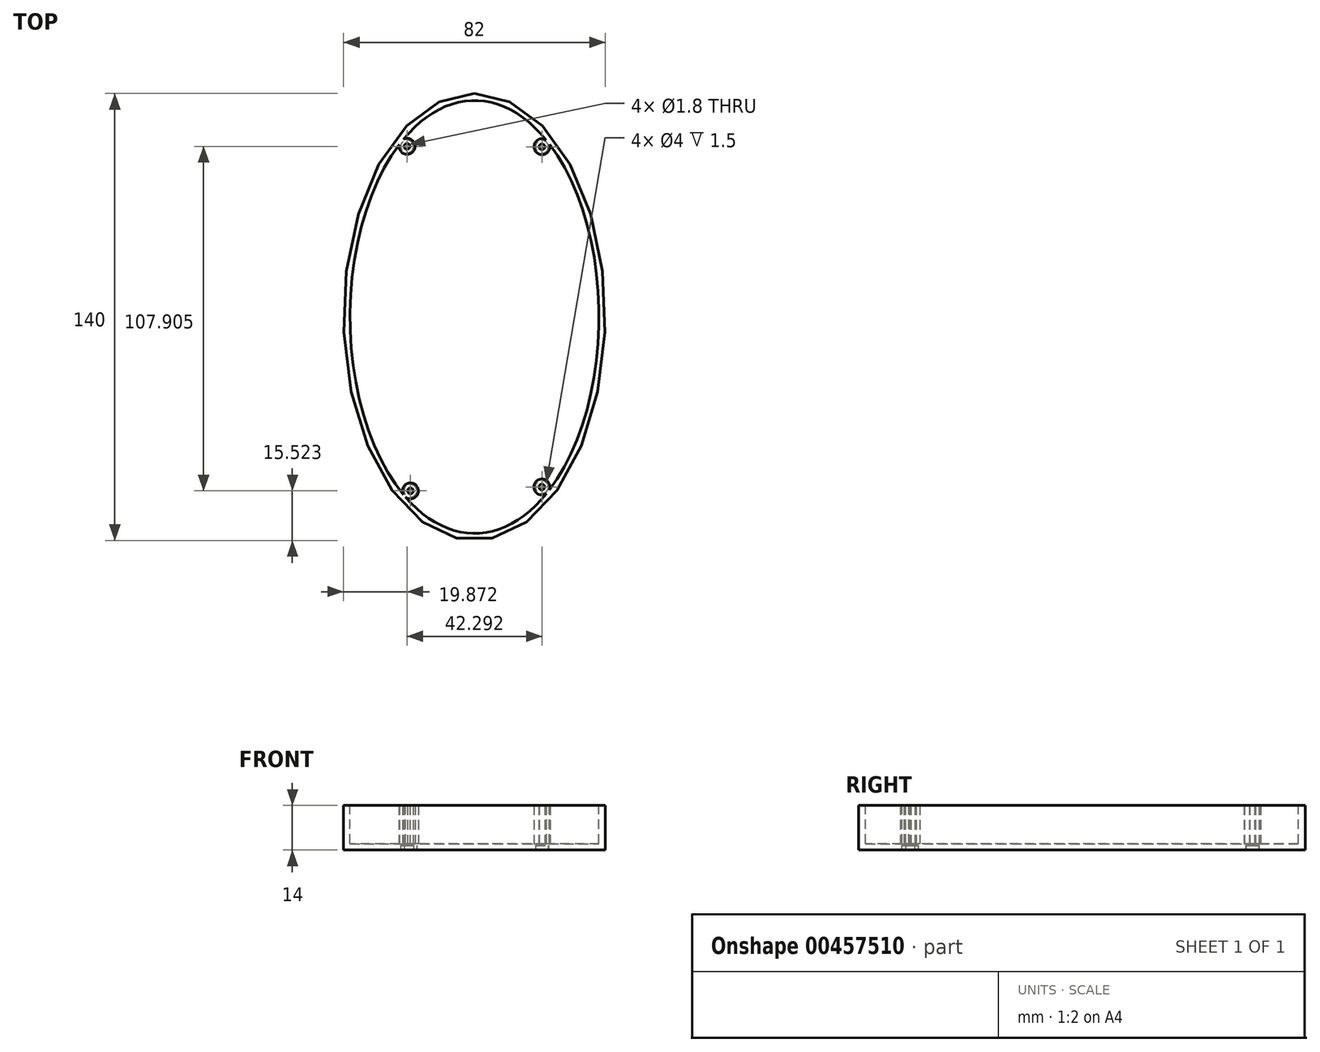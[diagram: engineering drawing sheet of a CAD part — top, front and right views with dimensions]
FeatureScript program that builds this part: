
annotation { "Feature Type Name" : "Feature", "Feature Type Description" : "" }
export const myFeature = defineFeature(function(context is Context, id is Id, definition is map)
    precondition{}
    {
        {
            var Q0;
            Q0=qCreatedBy(makeId("Top.planeOp"),FACE);
            var sketch = newSketch(context, id + "F0", { "sketchPlane" : qUnion([Q0])});
            skEllipse(sketch, "E0", {"center": v(-6.22, 3.26) * mm, "majorRadius": 70 * mm, "minorRadius": 41 * mm, "majorAxis": v(0, 1)});
            skSolve(sketch);
        }
        {
            var Q0;
            Q0 = qSketchRegion(id + "F2", true);
            var Q1;
            Q1 = qSketchRegion(id + "F0", true);
            extrude(context, id + "F1", {"entities" : qUnion([Q0, Q1]), "depth" : 17 * mm, "offsetDistance" : 25 * mm});
        }
        {
            var Q0;
            Q0=makeQuery(id+"F1.opExtrude","CAP_FACE",FACE,{"disambiguationData":[OSD([sQuery(id+"F0.wireOp",EDGE,"E0")])],"isStart":false});
            var sketch = newSketch(context, id + "F2", { "sketchPlane" : qUnion([Q0])});
            skEllipse(sketch, "E1", {"center": v(-6.22, 3.26) * mm, "majorRadius": 67.8 * mm, "minorRadius": 39 * mm, "majorAxis": v(0, 1)});
            skSolve(sketch);
        }
        {
            var Q0;
            Q0=makeQuery(id+"F2.imprint","IMPRINT",FACE,{"disambiguationData":[TD([[makeQuery(id+"F2.imprint","IMPRINT",EDGE,{"derivedFrom":sQuery(id+"F2.wireOp",EDGE,"E1")}),1.0]])]});
            extrude(context, id + "F3", {"entities" : qUnion([Q0]), "operationType" : NewBodyOperationType.REMOVE, "oppositeDirection" : true, "depth" : 15 * mm});
        }
        {
            var Q0;
            Q0=makeQuery(id+"F3.boolean.opBoolean","COPY",FACE,{"derivedFrom":makeQuery(id+"F3.opExtrude","CAP_FACE",FACE,{"disambiguationData":[OSD([sQuery(id+"F2.wireOp",EDGE,"E1")])],"isStart":false})});
            var sketch = newSketch(context, id + "F4", { "sketchPlane" : qUnion([Q0])});
            skCircle(sketch, "E2", {"center": v(-27.35, 56.69) * mm, "radius": 2.5 * mm});
            skPoint(sketch, "E2.first.point", {"position": v(-28.49, 58.91) * mm});
            skPoint(sketch, "E2.second.point", {"position": v(-26.1, 54.53) * mm});
            skPoint(sketch, "E2.third.point", {"position": v(-27.44, 54.19) * mm});
            skCircle(sketch, "E3", {"center": v(-27.35, 56.69) * mm, "radius": 0.9 * mm});
            skSolve(sketch);
        }
        {
            var Q0;
            {var subQ0=sQuery(id+"F4.wireOp",EDGE,"E2");var subQ1=makeQuery(id+"F3.boolean.opBoolean","COPY",EDGE,{"derivedFrom":makeQuery(id+"F3.opExtrude","CAP_EDGE",EDGE,{"disambiguationData":[OSD([sQuery(id+"F2.wireOp",EDGE,"E1")])],"isStart":false})});var subQ2=makeQuery(id+"F4.imprint","INTERSECT",VERTEX,{"disambiguationData":[OD(0.0)],"derivedFrom":[subQ1,subQ0]});Q0=makeQuery(id+"F4.imprint","IMPRINT",FACE,{"disambiguationData":[TD([[makeQuery(id+"F4.imprint","IMPRINT",EDGE,{"disambiguationData":[TD([[subQ2,-1.0]])],"derivedFrom":subQ0}),1.0]])]});}
            extrude(context, id + "F5", {"entities" : qUnion([Q0]), "operationType" : NewBodyOperationType.ADD, "depth" : 15 * mm});
        }
        {
            var Q0;
            Q0=makeQuery(id+"F3.boolean.opBoolean","COPY",FACE,{"derivedFrom":makeQuery(id+"F3.opExtrude","CAP_FACE",FACE,{"disambiguationData":[OSD([sQuery(id+"F2.wireOp",EDGE,"E1")])],"isStart":false})});
            var sketch = newSketch(context, id + "F6", { "sketchPlane" : qUnion([Q0])});
            skCircle(sketch, "E4", {"center": v(14.94, 56.58) * mm, "radius": 2.5 * mm});
            skPoint(sketch, "E4.first.point", {"position": v(12.51, 56) * mm});
            skPoint(sketch, "E4.second.point", {"position": v(17.34, 57.29) * mm});
            skPoint(sketch, "E4.third.point", {"position": v(16.01, 54.32) * mm});
            skCircle(sketch, "E5", {"center": v(14.94, 56.58) * mm, "radius": 0.9 * mm});
            skSolve(sketch);
        }
        {
            var Q0;
            {var subQ0=sQuery(id+"F6.wireOp",EDGE,"E4");var subQ1=makeQuery(id+"F3.boolean.opBoolean","COPY",EDGE,{"derivedFrom":makeQuery(id+"F3.opExtrude","CAP_EDGE",EDGE,{"disambiguationData":[OSD([sQuery(id+"F2.wireOp",EDGE,"E1")])],"isStart":false})});var subQ2=makeQuery(id+"F6.imprint","INTERSECT",VERTEX,{"disambiguationData":[OD(0.0)],"derivedFrom":[subQ1,subQ0]});Q0=makeQuery(id+"F6.imprint","IMPRINT",FACE,{"disambiguationData":[TD([[makeQuery(id+"F6.imprint","IMPRINT",EDGE,{"disambiguationData":[TD([[subQ2,1.0]])],"derivedFrom":subQ0}),1.0]])]});}
            extrude(context, id + "F7", {"entities" : qUnion([Q0]), "operationType" : NewBodyOperationType.ADD, "depth" : 15 * mm});
        }
        {
            var Q0;
            Q0=makeQuery(id+"F3.boolean.opBoolean","COPY",FACE,{"derivedFrom":makeQuery(id+"F3.opExtrude","CAP_FACE",FACE,{"disambiguationData":[OSD([sQuery(id+"F2.wireOp",EDGE,"E1")])],"isStart":false})});
            var sketch = newSketch(context, id + "F8", { "sketchPlane" : qUnion([Q0])});
            skCircle(sketch, "E6", {"center": v(-26.28, -51.22) * mm, "radius": 2.5 * mm});
            skPoint(sketch, "E6.first.point", {"position": v(-28.49, -50.03) * mm});
            skPoint(sketch, "E6.second.point", {"position": v(-24.98, -49.08) * mm});
            skPoint(sketch, "E6.third.point", {"position": v(-28.49, -52.4) * mm});
            skCircle(sketch, "E7", {"center": v(-26.28, -51.22) * mm, "radius": 0.9 * mm});
            skSolve(sketch);
        }
        {
            var Q0;
            {var subQ0=sQuery(id+"F8.wireOp",EDGE,"E6");var subQ1=makeQuery(id+"F7.boolean.opBoolean","SPLIT",EDGE,{"disambiguationData":[OD(0.0)],"derivedFrom":makeQuery(id+"F3.boolean.opBoolean","COPY",EDGE,{"derivedFrom":makeQuery(id+"F3.opExtrude","CAP_EDGE",EDGE,{"disambiguationData":[OSD([sQuery(id+"F2.wireOp",EDGE,"E1")])],"isStart":false})})});var subQ2=makeQuery(id+"F8.imprint","INTERSECT",VERTEX,{"disambiguationData":[OD(0.0)],"derivedFrom":[subQ1,subQ0]});Q0=makeQuery(id+"F8.imprint","IMPRINT",FACE,{"disambiguationData":[TD([[makeQuery(id+"F8.imprint","IMPRINT",EDGE,{"disambiguationData":[TD([[subQ2,1.0]])],"derivedFrom":subQ0}),1.0]])]});}
            extrude(context, id + "F9", {"entities" : qUnion([Q0]), "operationType" : NewBodyOperationType.ADD, "depth" : 15 * mm});
        }
        {
            var Q0;
            Q0=makeQuery(id+"F3.boolean.opBoolean","COPY",FACE,{"derivedFrom":makeQuery(id+"F3.opExtrude","CAP_FACE",FACE,{"disambiguationData":[OSD([sQuery(id+"F2.wireOp",EDGE,"E1")])],"isStart":false})});
            var sketch = newSketch(context, id + "F10", { "sketchPlane" : qUnion([Q0])});
            skCircle(sketch, "E8", {"center": v(14.89, -50.02) * mm, "radius": 2.5 * mm});
            skPoint(sketch, "E8.first.point", {"position": v(17.2, -50.95) * mm});
            skPoint(sketch, "E8.second.point", {"position": v(12.45, -49.45) * mm});
            skPoint(sketch, "E8.third.point", {"position": v(13.95, -47.7) * mm});
            skCircle(sketch, "E9", {"center": v(14.89, -50.02) * mm, "radius": 0.9 * mm});
            skSolve(sketch);
        }
        {
            var Q0;
            {var subQ0=sQuery(id+"F10.wireOp",EDGE,"E8");var subQ1=sQuery(id+"F2.wireOp",EDGE,"E1");var subQ2=makeQuery(id+"F9.boolean.opBoolean","SPLIT",EDGE,{"disambiguationData":[TD([makeQuery(id+"F7.opExtrude","SWEPT_FACE",FACE,{"disambiguationData":[OSD([sQuery(id+"F6.wireOp",EDGE,"E4")])]})])],"derivedFrom":makeQuery(id+"F7.boolean.opBoolean","SPLIT",EDGE,{"disambiguationData":[OD(0.0)],"derivedFrom":makeQuery(id+"F3.boolean.opBoolean","COPY",EDGE,{"derivedFrom":makeQuery(id+"F3.opExtrude","CAP_EDGE",EDGE,{"disambiguationData":[OSD([subQ1])],"isStart":false})})})});var subQ3=makeQuery(id+"F10.imprint","INTERSECT",VERTEX,{"disambiguationData":[OD(0.0)],"derivedFrom":[subQ2,subQ0]});Q0=makeQuery(id+"F10.imprint","IMPRINT",FACE,{"disambiguationData":[TD([[makeQuery(id+"F10.imprint","IMPRINT",EDGE,{"disambiguationData":[TD([[subQ3,-1.0]])],"derivedFrom":subQ0}),1.0]])]});}
            extrude(context, id + "F11", {"entities" : qUnion([Q0]), "operationType" : NewBodyOperationType.ADD, "depth" : 15 * mm});
        }
        {
            var Q0;
            {var subQ0=sQuery(id+"F2.wireOp",EDGE,"E1");Q0=makeQuery(id+"F11.boolean.opBoolean","MERGE",FACE,{"derivedFrom":[makeQuery(id+"F9.boolean.opBoolean","MERGE",FACE,{"derivedFrom":[makeQuery(id+"F7.boolean.opBoolean","MERGE",FACE,{"derivedFrom":[makeQuery(id+"F5.boolean.opBoolean","MERGE",FACE,{"derivedFrom":[makeQuery(id+"F1.opExtrude","CAP_FACE",FACE,{"disambiguationData":[OSD([sQuery(id+"F0.wireOp",EDGE,"E0")])],"isStart":false}),makeQuery(id+"F5.opExtrude","CAP_FACE",FACE,{"disambiguationData":[OSD([subQ0,sQuery(id+"F4.wireOp",EDGE,"E2")])],"isStart":false})]}),makeQuery(id+"F7.opExtrude","CAP_FACE",FACE,{"disambiguationData":[OSD([subQ0,sQuery(id+"F6.wireOp",EDGE,"E4")])],"isStart":false})]}),makeQuery(id+"F9.opExtrude","CAP_FACE",FACE,{"disambiguationData":[OSD([subQ0,sQuery(id+"F8.wireOp",EDGE,"E6")])],"isStart":false})]}),makeQuery(id+"F11.opExtrude","CAP_FACE",FACE,{"disambiguationData":[OSD([subQ0,sQuery(id+"F10.wireOp",EDGE,"E8")])],"isStart":false})]});}
            var sketch = newSketch(context, id + "F12", { "sketchPlane" : qUnion([Q0])});
            skSolve(sketch);
        }
        {
            var Q0;
            {var subQ8=sQuery(id+"F0.wireOp",EDGE,"E0");Q0=makeQuery(id+"F12.imprint","IMPRINT",FACE,{"disambiguationData":[TD([[makeQuery(id+"F12.imprint","IMPRINT",EDGE,{"derivedFrom":makeQuery(id+"F1.opExtrude","CAP_EDGE",EDGE,{"disambiguationData":[OSD([subQ8])],"isStart":false})}),1.0]])]});}
            var sketch = newSketch(context, id + "F13", { "sketchPlane" : qUnion([Q0])});
            skCircle(sketch, "E10.0", {"center": v(-27.35, 56.69) * mm, "radius": 0.9 * mm});
            skCircle(sketch, "E11.0", {"center": v(14.94, 56.58) * mm, "radius": 0.9 * mm});
            skCircle(sketch, "E12.0", {"center": v(-26.28, -51.22) * mm, "radius": 0.9 * mm});
            skCircle(sketch, "E13.0", {"center": v(14.89, -50.02) * mm, "radius": 0.9 * mm});
            skSolve(sketch);
        }
        {
            var Q0;
            Q0 = qSketchRegion(id + "F13", true);
            extrude(context, id + "F14", {"entities" : qUnion([Q0]), "operationType" : NewBodyOperationType.REMOVE, "endBound" : BoundingType.THROUGH_ALL, "oppositeDirection" : true, "depth" : 25 * mm});
        }
        {
            var Q0;
            Q0=makeQuery(id+"F1.opExtrude","CAP_FACE",FACE,{"disambiguationData":[OSD([sQuery(id+"F0.wireOp",EDGE,"E0")])],"isStart":true});
            var sketch = newSketch(context, id + "F15", { "sketchPlane" : qUnion([Q0])});
            skCircle(sketch, "E14", {"center": v(14.94, -56.58) * mm, "radius": 2 * mm});
            skCircle(sketch, "E15", {"center": v(-27.35, -56.69) * mm, "radius": 2 * mm});
            skCircle(sketch, "E16", {"center": v(-26.28, 51.22) * mm, "radius": 2 * mm});
            skCircle(sketch, "E17", {"center": v(14.89, 50.02) * mm, "radius": 2 * mm});
            skSolve(sketch);
        }
        {
            var Q0;
            Q0 = qSketchRegion(id + "F15", true);
            extrude(context, id + "F16", {"entities" : qUnion([Q0]), "operationType" : NewBodyOperationType.REMOVE, "oppositeDirection" : true, "depth" : 1.5 * mm, "offsetDistance" : 25 * mm});
        }
        {
            var Q0;
            {var subQ8=sQuery(id+"F0.wireOp",EDGE,"E0");Q0=makeQuery(id+"F12.imprint","IMPRINT",FACE,{"disambiguationData":[TD([[makeQuery(id+"F12.imprint","IMPRINT",EDGE,{"derivedFrom":makeQuery(id+"F1.opExtrude","CAP_EDGE",EDGE,{"disambiguationData":[OSD([subQ8])],"isStart":false})}),1.0]])]});}
            extrude(context, id + "F17", {"entities" : qUnion([Q0]), "operationType" : NewBodyOperationType.REMOVE, "oppositeDirection" : true, "depth" : 3 * mm, "offsetDistance" : 25 * mm});
        }
    });
